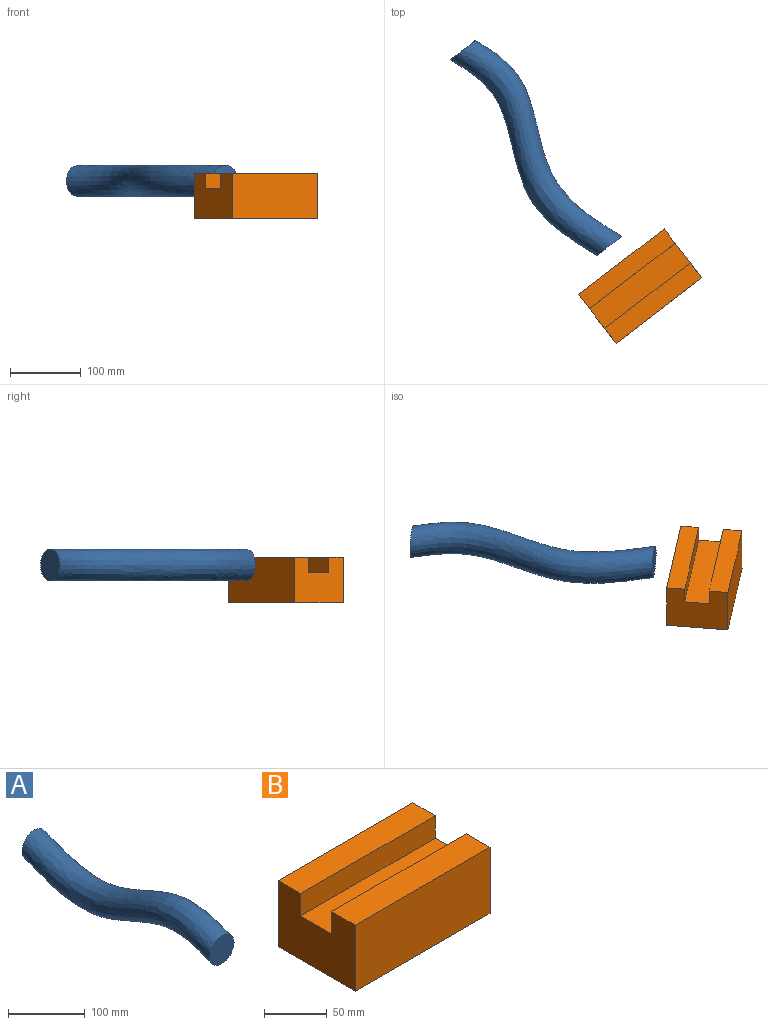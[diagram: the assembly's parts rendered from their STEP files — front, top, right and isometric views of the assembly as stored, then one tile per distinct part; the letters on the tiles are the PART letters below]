
ASSEMBLY  parts=2 mates=1
PART A: 3 faces, bbox 89.5x345.6x94.9 mm
  f0: plane 44.75x44.75mm, normal (0,-1,0), area 1573.1mm2, adj f2
  f1: plane 44.75x44.75mm, normal (0,1,0), area 1573.1mm2, adj f2
  f2: bspline ~345.59x94.86mm, area 49646.3mm2, adj f0,f1
PART B: 10 faces, bbox 152.4x87.2x64.7 mm
  f0: plane 152.4x26.69mm, normal (0,0,1), area 4068.2mm2, adj f1,f7,f8,f9
  f1: plane 152.4x64.65mm, normal (0,-1,0), area 9853mm2, adj f0,f2,f8,f9
  f2: plane 152.4x87.24mm, normal (0,0,-1), area 13295.1mm2, adj f1,f3,f8,f9
  f3: plane 152.4x64.65mm, normal (0,1,0), area 9853mm2, adj f2,f4,f8,f9
  f4: plane 152.4x25.4mm, normal (0,0,1), area 3870.5mm2, adj f3,f5,f8,f9
  f5: plane 152.4x21.93mm, normal (0,-1,0), area 3342.8mm2, adj f4,f6,f8,f9
  f6: plane 152.4x35.15mm, normal (0,0,1), area 5356.4mm2, adj f5,f7,f8,f9
  f7: plane 152.4x21.93mm, normal (0,1,0), area 3342.8mm2, adj f0,f6,f8,f9
  f8: plane 87.24x64.65mm, normal (1,0,0), area 4869.2mm2, adj f0,f1,f2,f3,f4,f5,f6,f7
  f9: plane 87.24x64.65mm, normal (-1,0,0), area 4869.2mm2, adj f0,f1,f2,f3,f4,f5,f6,f7
PLACE A rot(axis=(-0.69,-0.23,-0.69),153.7deg) t=(-240.71,277.8,47.54)mm
PLACE B rot(axis=(0,0,1),37.5deg) t=(-48.87,-104.37,27.63)mm
MATE slider A.f1 <-> B.f5  axis (0.61,-0.79,0) through (-33.69,1.05,47.54)mm
